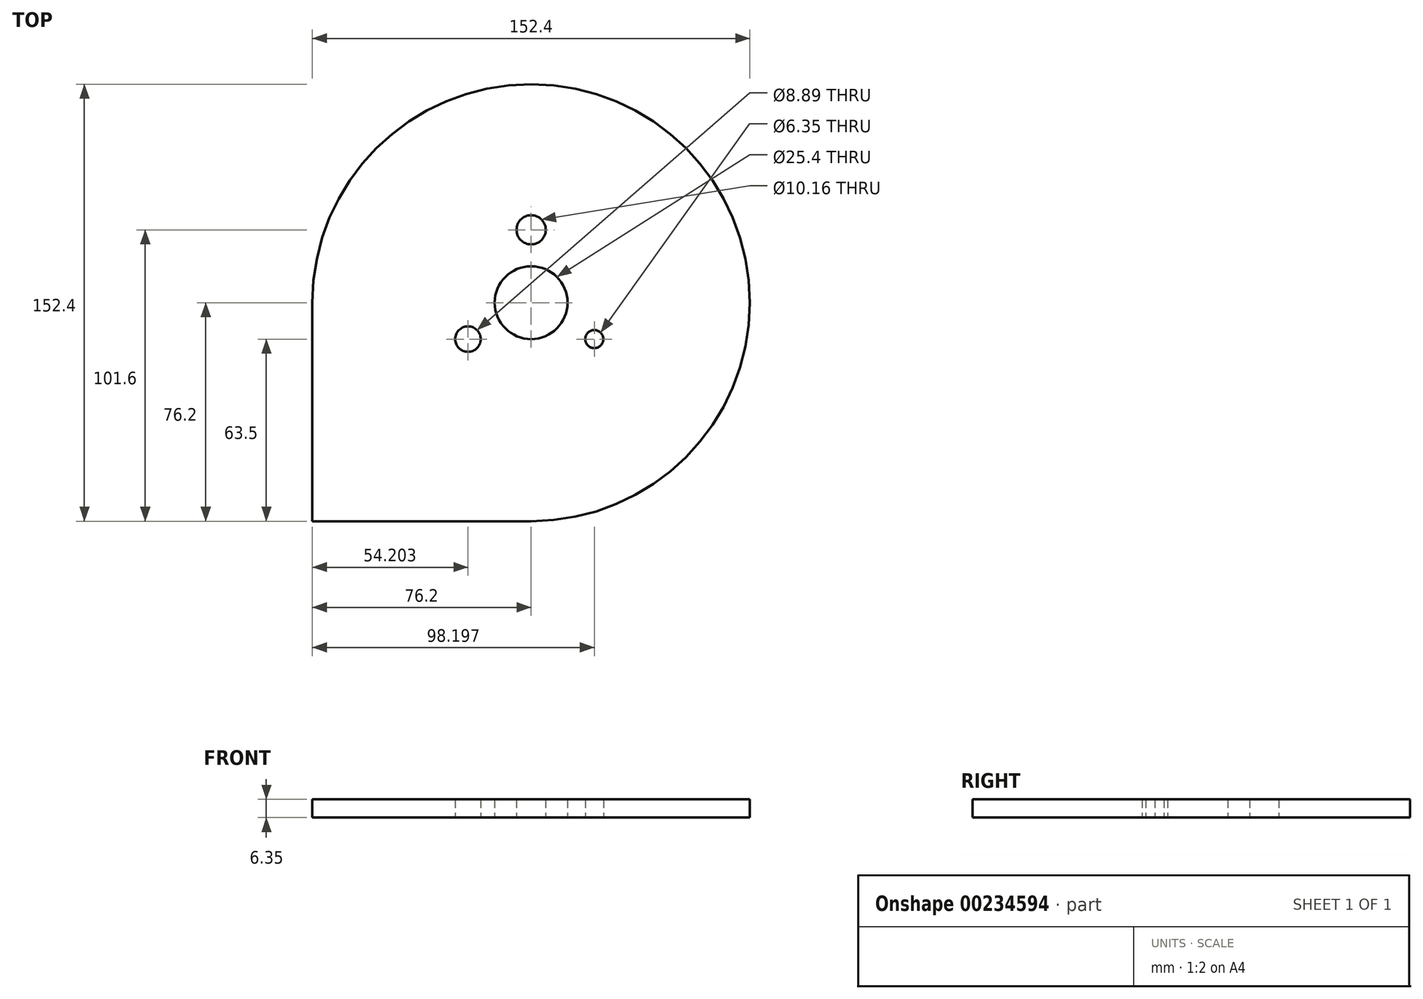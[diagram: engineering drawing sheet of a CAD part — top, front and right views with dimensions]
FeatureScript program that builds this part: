
annotation { "Feature Type Name" : "Feature", "Feature Type Description" : "" }
export const myFeature = defineFeature(function(context is Context, id is Id, definition is map)
    precondition{}
    {
        {
            var Q0;
            Q0=qCreatedBy(makeId("Top.planeOp"),FACE);
            var sketch = newSketch(context, id + "F0", { "sketchPlane" : qUnion([Q0])});
            skLineSegment(sketch, "E0.top", {"start": v(38.1, -38.1) * mm, "end": v(-38.1, -38.1) * mm});
            skLineSegment(sketch, "E0.right", {"start": v(-38.1, 38.1) * mm, "end": v(-38.1, -38.1) * mm});
            skPoint(sketch, "E0.middle", {"position": v(0, 0) * mm});
            skPoint(sketch, "E0.left.start.orphan", {"position": v(38.1, 38.1) * mm});
            skArc(sketch, "E1", {"start": v(38.1, -38.1) * mm, "mid": v(91.98, 91.98) * mm, "end": v(-38.1, 38.1) * mm});
            skCircle(sketch, "E2.cCircle", {"center": v(38.1, 38.1) * mm, "radius": 12.7 * mm, "construction": true});
            skLineSegment(sketch, "E2.0", {"start": v(60.1, 25.4) * mm, "end": v(16.1, 25.4) * mm, "construction": true});
            skLineSegment(sketch, "E2.1", {"start": v(16.1, 25.4) * mm, "end": v(38.1, 63.5) * mm, "construction": true});
            skLineSegment(sketch, "E2.2", {"start": v(38.1, 63.5) * mm, "end": v(60.1, 25.4) * mm, "construction": true});
            skPoint(sketch, "E2.0.midPoint", {"position": v(38.1, 25.4) * mm});
            skCircle(sketch, "E3", {"center": v(38.1, 38.1) * mm, "radius": 6.35 * mm});
            skCircle(sketch, "E4.0", {"center": v(38.1, 38.1) * mm, "radius": 12.7 * mm});
            skCircle(sketch, "E5", {"center": v(60.1, 25.4) * mm, "radius": 3.18 * mm});
            skCircle(sketch, "E6", {"center": v(16.1, 25.4) * mm, "radius": 4.45 * mm});
            skCircle(sketch, "E7", {"center": v(38.1, 63.5) * mm, "radius": 5.08 * mm});
            skSolve(sketch);
        }
        {
            var Q0;
            Q0=makeQuery(id+"F0.imprint","IMPRINT",FACE,{"disambiguationData":[TD([[makeQuery(id+"F0.imprint","IMPRINT",EDGE,{"derivedFrom":sQuery(id+"F0.wireOp",EDGE,"E0.top")}),-1.0]])]});
            extrude(context, id + "F1", {"entities" : qUnion([Q0]), "depth" : 6.35 * mm});
        }
    });
